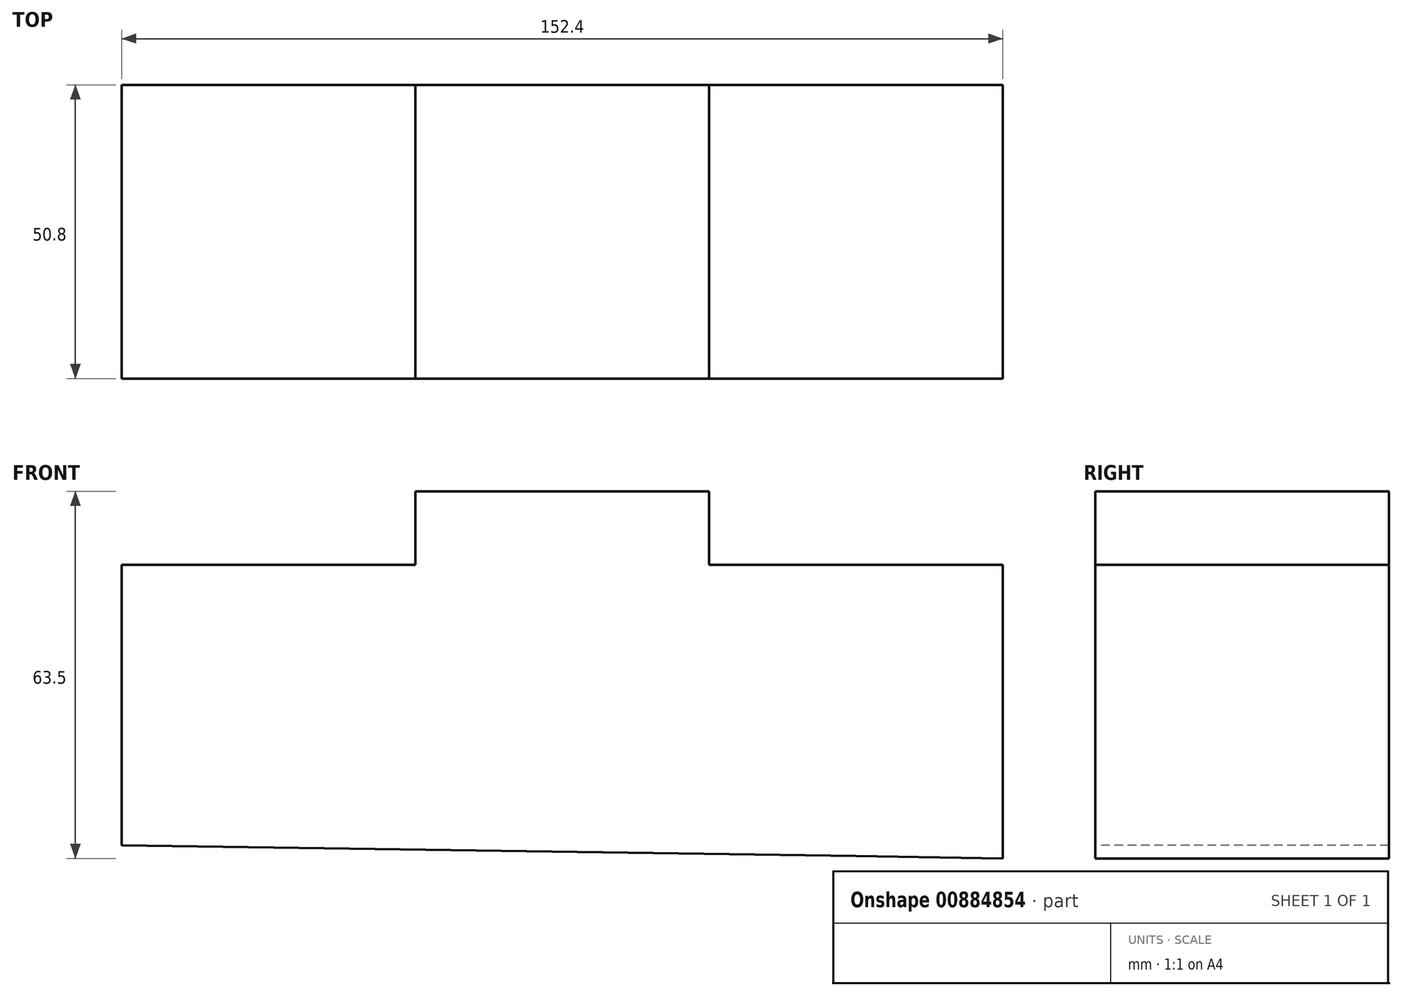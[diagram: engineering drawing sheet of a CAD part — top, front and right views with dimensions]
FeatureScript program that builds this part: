
annotation { "Feature Type Name" : "Feature", "Feature Type Description" : "" }
export const myFeature = defineFeature(function(context is Context, id is Id, definition is map)
    precondition{}
    {
        {
            var Q0;
            Q0=qCreatedBy(makeId("Front.planeOp"),FACE);
            var sketch = newSketch(context, id + "F0", { "sketchPlane" : qUnion([Q0])});
            skLineSegment(sketch, "E0", {"start": v(29.79, -53.3) * mm, "end": v(55.2, -53.71) * mm});
            skLineSegment(sketch, "E1", {"start": v(55.2, -53.71) * mm, "end": v(55.2, -2.91) * mm});
            skLineSegment(sketch, "E2", {"start": v(55.2, -2.91) * mm, "end": v(4.4, -2.91) * mm});
            skLineSegment(sketch, "E3", {"start": v(4.4, -2.91) * mm, "end": v(4.4, 9.79) * mm});
            skLineSegment(sketch, "E4", {"start": v(4.4, 9.79) * mm, "end": v(-46.4, 9.79) * mm});
            skLineSegment(sketch, "E5", {"start": v(-46.4, 9.79) * mm, "end": v(-46.4, -2.91) * mm});
            skLineSegment(sketch, "E6", {"start": v(-46.4, -2.91) * mm, "end": v(-97.2, -2.91) * mm});
            skLineSegment(sketch, "E7", {"start": v(-97.2, -2.91) * mm, "end": v(-97.2, -51.45) * mm});
            skLineSegment(sketch, "E8", {"start": v(-97.2, -51.45) * mm, "end": v(29.79, -53.3) * mm});
            skSolve(sketch);
        }
        {
            var Q0;
            Q0 = qSketchRegion(id + "F0", true);
            extrude(context, id + "F1", {"entities" : qUnion([Q0]), "oppositeDirection" : true, "depth" : 50.8 * mm, "offsetDistance" : 25.4 * mm});
        }
    });
